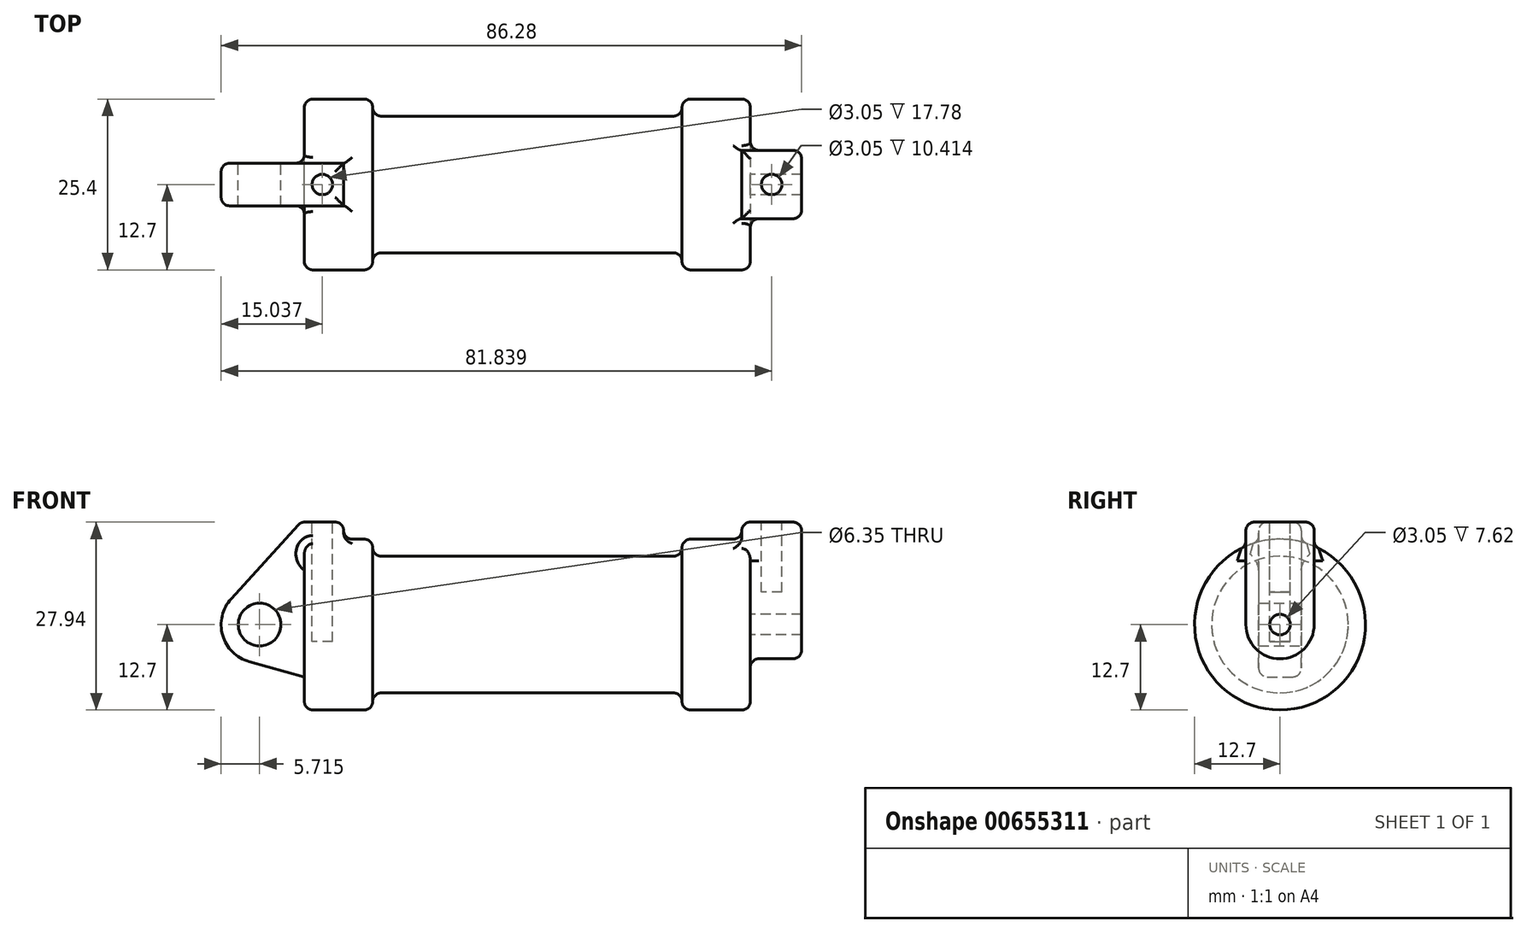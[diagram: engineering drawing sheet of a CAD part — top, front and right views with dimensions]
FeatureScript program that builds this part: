
annotation { "Feature Type Name" : "Feature", "Feature Type Description" : "" }
export const myFeature = defineFeature(function(context is Context, id is Id, definition is map)
    precondition{}
    {
        {
            var Q0;
            Q0=qCreatedBy(makeId("Front.planeOp"),FACE);
            var sketch = newSketch(context, id + "F0", { "sketchPlane" : qUnion([Q0])});
            skLineSegment(sketch, "E0", {"start": v(0, 0) * mm, "end": v(0, 12.7) * mm});
            skLineSegment(sketch, "E1", {"start": v(0, 12.7) * mm, "end": v(10.16, 12.7) * mm});
            skLineSegment(sketch, "E2", {"start": v(10.16, 12.7) * mm, "end": v(10.16, 10.16) * mm});
            skLineSegment(sketch, "E3", {"start": v(10.16, 10.16) * mm, "end": v(56.13, 10.16) * mm});
            skLineSegment(sketch, "E4", {"start": v(56.13, 10.16) * mm, "end": v(56.13, 12.7) * mm});
            skLineSegment(sketch, "E5", {"start": v(56.13, 12.7) * mm, "end": v(66.3, 12.7) * mm});
            skLineSegment(sketch, "E6", {"start": v(66.3, 12.7) * mm, "end": v(66.3, 0) * mm});
            skLineSegment(sketch, "E7", {"start": v(66.3, 0) * mm, "end": v(0, 0) * mm});
            skLineSegment(sketch, "E8", {"start": v(5.84, 15.24) * mm, "end": v(-0.5, 15.24) * mm});
            skLineSegment(sketch, "E9", {"start": v(-0.5, 15.24) * mm, "end": v(-10.88, 3.85) * mm});
            skLineSegment(sketch, "E10", {"start": v(0, 0) * mm, "end": v(-6.65, 0) * mm});
            skCircle(sketch, "E11", {"center": v(-6.65, 0) * mm, "radius": 5.72 * mm});
            skCircle(sketch, "E12", {"center": v(-6.65, 0) * mm, "radius": 3.18 * mm});
            skLineSegment(sketch, "E13", {"start": v(5.84, 15.24) * mm, "end": v(5.84, -9.4) * mm});
            skLineSegment(sketch, "E14", {"start": v(5.84, -9.4) * mm, "end": v(-8.18, -5.5) * mm});
            skSolve(sketch);
        }
        {
            var Q0;
            {var subQ0=sQuery(id+"F0.wireOp",EDGE,"E0");Q0=makeQuery(id+"F0.imprint","IMPRINT",FACE,{"disambiguationData":[TD([[makeQuery(id+"F0.imprint","IMPRINT",EDGE,{"derivedFrom":subQ0}),-1.0]])]});}
            var Q1;
            {var subQ0=sQuery(id+"F0.wireOp",EDGE,"E2");Q1=makeQuery(id+"F0.imprint","IMPRINT",FACE,{"disambiguationData":[TD([[makeQuery(id+"F0.imprint","IMPRINT",EDGE,{"derivedFrom":subQ0}),-1.0]])]});}
            var Q2;
            Q2=sQuery(id+"F0.wireOp",EDGE,"E7");
            revolve(context, id + "F1", {"entities" : qUnion([Q0, Q1]), "axis" : qUnion([Q2]), "revolveType" : RevolveType.FULL});
        }
        {
            var Q0;
            {var subQ0=sQuery(id+"F0.wireOp",EDGE,"E0");Q0=makeQuery(id+"F0.imprint","IMPRINT",FACE,{"disambiguationData":[TD([[makeQuery(id+"F0.imprint","IMPRINT",EDGE,{"derivedFrom":subQ0}),-1.0]])]});}
            var Q1;
            {var subQ1=sQuery(id+"F0.wireOp",EDGE,"E0");Q1=makeQuery(id+"F0.imprint","IMPRINT",FACE,{"disambiguationData":[TD([[makeQuery(id+"F0.imprint","IMPRINT",EDGE,{"derivedFrom":subQ1}),1.0]])]});}
            var Q2;
            {var subQ0=sQuery(id+"F0.wireOp",EDGE,"E14");Q2=makeQuery(id+"F0.imprint","IMPRINT",FACE,{"disambiguationData":[TD([[makeQuery(id+"F0.imprint","IMPRINT",EDGE,{"derivedFrom":subQ0}),-1.0]])]});}
            var Q3;
            {var subQ5=sQuery(id+"F0.wireOp",EDGE,"E12");Q3=makeQuery(id+"F0.imprint","IMPRINT",FACE,{"disambiguationData":[TD([[makeQuery(id+"F0.imprint","IMPRINT",EDGE,{"derivedFrom":subQ5}),-1.0]])]});}
            extrude(context, id + "F2", {"entities" : qUnion([Q0, Q1, Q2, Q3]), "operationType" : NewBodyOperationType.ADD, "endBound" : BoundingType.SYMMETRIC, "depth" : 6.35 * mm, "offsetDistance" : 25.4 * mm});
        }
        {
            var Q0;
            Q0=makeQuery(id+"F1.opRevolve","SWEPT_FACE",FACE,{"disambiguationData":[OSD([sQuery(id+"F0.wireOp",EDGE,"E6")])]});
            var sketch = newSketch(context, id + "F3", { "sketchPlane" : qUnion([Q0])});
            skCircle(sketch, "E15", {"center": v(0, 0) * mm, "radius": 5.08 * mm});
            skCircle(sketch, "E16", {"center": v(0, 0) * mm, "radius": 1.52 * mm});
            skLineSegment(sketch, "E17", {"start": v(-5.08, 0) * mm, "end": v(-5.08, 15.24) * mm});
            skLineSegment(sketch, "E18", {"start": v(-5.08, 15.24) * mm, "end": v(5.08, 15.24) * mm});
            skLineSegment(sketch, "E19", {"start": v(5.08, 15.24) * mm, "end": v(5.08, 0) * mm});
            skSolve(sketch);
        }
        {
            var Q0;
            {var subQ0=sQuery(id+"F3.wireOp",EDGE,"E17");var subQ1=sQuery(id+"F3.wireOp",EDGE,"E15");var subQ2=makeQuery(id+"F3.imprint","INTERSECT",VERTEX,{"derivedFrom":[subQ1,subQ0]});Q0=makeQuery(id+"F3.imprint","IMPRINT",FACE,{"disambiguationData":[TD([[makeQuery(id+"F3.imprint","IMPRINT",EDGE,{"disambiguationData":[TD([[subQ2,1.0]])],"derivedFrom":subQ1}),-1.0]])]});}
            var Q1;
            {var subQ0=sQuery(id+"F3.wireOp",EDGE,"E18");Q1=makeQuery(id+"F3.imprint","IMPRINT",FACE,{"disambiguationData":[TD([[makeQuery(id+"F3.imprint","IMPRINT",EDGE,{"derivedFrom":subQ0}),-1.0]])]});}
            var Q2;
            Q2=makeQuery(id+"F3.imprint","IMPRINT",FACE,{"disambiguationData":[TD([[makeQuery(id+"F3.imprint","IMPRINT",EDGE,{"derivedFrom":sQuery(id+"F3.wireOp",EDGE,"E16")}),-1.0]])]});
            extrude(context, id + "F4", {"entities" : qUnion([Q0, Q1, Q2]), "operationType" : NewBodyOperationType.ADD, "depth" : 7.62 * mm, "offsetDistance" : 25.4 * mm, "hasSecondDirection" : true, "secondDirectionOppositeDirection" : true, "secondDirectionDepth" : 1.27 * mm});
        }
        {
            var Q0;
            Q0=makeQuery(id+"F3.imprint","IMPRINT",FACE,{"disambiguationData":[TD([[makeQuery(id+"F3.imprint","IMPRINT",EDGE,{"derivedFrom":sQuery(id+"F3.wireOp",EDGE,"E16")}),1.0]])]});
            var Q1;
            Q1=makeQuery(id+"F1.opRevolve","SWEPT_FACE",FACE,{"disambiguationData":[OSD([sQuery(id+"F0.wireOp",EDGE,"E2")])]});
            extrude(context, id + "F5", {"entities" : qUnion([Q0]), "operationType" : NewBodyOperationType.ADD, "endBound" : BoundingType.UP_TO_SURFACE, "oppositeDirection" : true, "depth" : 25.4 * mm, "endBoundEntityFace" : qUnion([Q1]), "offsetDistance" : 25.4 * mm});
        }
        {
            var Q0;
            Q0=makeQuery(id+"F4.opExtrude","SWEPT_FACE",FACE,{"disambiguationData":[OSD([sQuery(id+"F3.wireOp",EDGE,"E18")])]});
            var sketch = newSketch(context, id + "F6", { "sketchPlane" : qUnion([Q0])});
            skCircle(sketch, "E20", {"center": v(69.47, 0) * mm, "radius": 1.52 * mm});
            skPoint(sketch, "E20.centerSnap0", {"position": v(69.47, 5.08) * mm});
            skPoint(sketch, "E20.centerSnap1", {"position": v(73.91, 0) * mm});
            skCircle(sketch, "E21", {"center": v(2.67, 0) * mm, "radius": 1.52 * mm});
            skSolve(sketch);
        }
        {
            var Q0;
            Q0=makeQuery(id+"F6.imprint","IMPRINT",FACE,{"disambiguationData":[TD([[makeQuery(id+"F6.imprint","IMPRINT",EDGE,{"derivedFrom":sQuery(id+"F6.wireOp",EDGE,"E21")}),1.0]])]});
            extrude(context, id + "F7", {"entities" : qUnion([Q0]), "operationType" : NewBodyOperationType.REMOVE, "oppositeDirection" : true, "depth" : 17.78 * mm, "offsetDistance" : 25.4 * mm});
        }
        {
            var Q0;
            Q0=makeQuery(id+"F6.imprint","IMPRINT",FACE,{"disambiguationData":[TD([[makeQuery(id+"F6.imprint","IMPRINT",EDGE,{"derivedFrom":sQuery(id+"F6.wireOp",EDGE,"E20")}),1.0]])]});
            extrude(context, id + "F8", {"entities" : qUnion([Q0]), "operationType" : NewBodyOperationType.REMOVE, "oppositeDirection" : true, "depth" : 10.4 * mm, "offsetDistance" : 25.4 * mm});
        }
        {
            var Q0;
            Q0=makeQuery(id+"F1.opRevolve","SWEPT_FACE",FACE,{"disambiguationData":[OSD([sQuery(id+"F0.wireOp",EDGE,"E3")])]});
            var Q1;
            Q1=makeQuery(id+"F1.opRevolve","SWEPT_FACE",FACE,{"disambiguationData":[OSD([sQuery(id+"F0.wireOp",EDGE,"E1")])]});
            var Q2;
            Q2=makeQuery(id+"F1.opRevolve","SWEPT_EDGE",EDGE,{"disambiguationData":[OSD([sQuery(id+"F0.wireOp",EDGE,"E4"),sQuery(id+"F0.wireOp",EDGE,"E5")])]});
            var Q3;
            Q3=makeQuery(id+"F1.opRevolve","SWEPT_EDGE",EDGE,{"disambiguationData":[OSD([sQuery(id+"F0.wireOp",EDGE,"E5"),sQuery(id+"F0.wireOp",EDGE,"E6")])]});
            fillet(context, id + "F9", {"entities" : qUnion([Q0, Q1, Q2, Q3]), "radius" : 1.27 * mm, "tangentPropagation" : true, "allowEdgeOverflow" : false});
        }
        {
            var Q0;
            Q0=makeQuery(id+"F9.opFillet","BLEND_EDGE",EDGE,{"blendedFrom":[makeQuery(id+"F1.opRevolve","SWEPT_EDGE",EDGE,{"disambiguationData":[OSD([sQuery(id+"F0.wireOp",EDGE,"E5"),sQuery(id+"F0.wireOp",EDGE,"E6")])]}),makeQuery(id+"F4.opExtrude","SWEPT_FACE",FACE,{"disambiguationData":[OSD([sQuery(id+"F3.wireOp",EDGE,"E17")])]})],"blendedInto":[makeQuery(id+"F4.opExtrude","SWEPT_FACE",FACE,{"disambiguationData":[OSD([sQuery(id+"F3.wireOp",EDGE,"E17")])]})]});
            var Q1;
            Q1=makeQuery(id+"F4.opExtrude","CAP_EDGE",EDGE,{"disambiguationData":[OSD([sQuery(id+"F3.wireOp",EDGE,"E15")])],"isStart":false});
            var Q2;
            Q2=makeQuery(id+"F4.opExtrude","SWEPT_EDGE",EDGE,{"disambiguationData":[OSD([sQuery(id+"F3.wireOp",EDGE,"E17"),sQuery(id+"F3.wireOp",EDGE,"E18")])]});
            var Q3;
            Q3=makeQuery(id+"F4.opExtrude","CAP_EDGE",EDGE,{"disambiguationData":[OSD([sQuery(id+"F3.wireOp",EDGE,"E18")])],"isStart":true});
            var Q4;
            Q4=makeQuery(id+"F4.opExtrude","SWEPT_EDGE",EDGE,{"disambiguationData":[OSD([sQuery(id+"F3.wireOp",EDGE,"E18"),sQuery(id+"F3.wireOp",EDGE,"E19")])]});
            var Q5;
            Q5=makeQuery(id+"F4.opExtrude","CAP_EDGE",EDGE,{"disambiguationData":[OSD([sQuery(id+"F3.wireOp",EDGE,"E18")])],"isStart":false});
            var Q6;
            Q6=makeQuery(id+"F4.boolean.opBoolean","INTERSECT",EDGE,{"derivedFrom":[makeQuery(id+"F1.opRevolve","SWEPT_FACE",FACE,{"disambiguationData":[OSD([sQuery(id+"F0.wireOp",EDGE,"E5")])]}),makeQuery(id+"F4.opExtrude","CAP_FACE",FACE,{"disambiguationData":[OSD([sQuery(id+"F3.wireOp",EDGE,"E15"),sQuery(id+"F3.wireOp",EDGE,"E16"),sQuery(id+"F3.wireOp",EDGE,"E17"),sQuery(id+"F3.wireOp",EDGE,"E18"),sQuery(id+"F3.wireOp",EDGE,"E19")])],"isStart":true})]});
            fillet(context, id + "F10", {"entities" : qUnion([Q0, Q1, Q2, Q3, Q4, Q5, Q6]), "radius" : 1.27 * mm, "tangentPropagation" : true, "allowEdgeOverflow" : false});
        }
        {
            var Q0;
            Q0=makeQuery(id+"F2.opExtrude","CAP_EDGE",EDGE,{"disambiguationData":[OSD([sQuery(id+"F0.wireOp",EDGE,"E9")])],"isStart":false});
            var Q1;
            Q1=makeQuery(id+"F2.opExtrude","CAP_EDGE",EDGE,{"disambiguationData":[OSD([sQuery(id+"F0.wireOp",EDGE,"E9")])],"isStart":true});
            var Q2;
            Q2=makeQuery(id+"F2.opExtrude","SWEPT_EDGE",EDGE,{"disambiguationData":[OSD([sQuery(id+"F0.wireOp",EDGE,"E8"),sQuery(id+"F0.wireOp",EDGE,"E9")])]});
            var Q3;
            Q3=makeQuery(id+"F2.opExtrude","CAP_EDGE",EDGE,{"disambiguationData":[OSD([sQuery(id+"F0.wireOp",EDGE,"E8")])],"isStart":false});
            var Q4;
            Q4=makeQuery(id+"F2.opExtrude","SWEPT_EDGE",EDGE,{"disambiguationData":[OSD([sQuery(id+"F0.wireOp",EDGE,"E8"),sQuery(id+"F0.wireOp",EDGE,"E13")])]});
            var Q5;
            Q5=makeQuery(id+"F2.opExtrude","CAP_EDGE",EDGE,{"disambiguationData":[OSD([sQuery(id+"F0.wireOp",EDGE,"E8")])],"isStart":true});
            fillet(context, id + "F11", {"entities" : qUnion([Q0, Q1, Q2, Q3, Q4, Q5]), "radius" : 1.27 * mm, "tangentPropagation" : true, "allowEdgeOverflow" : false});
        }
    });
